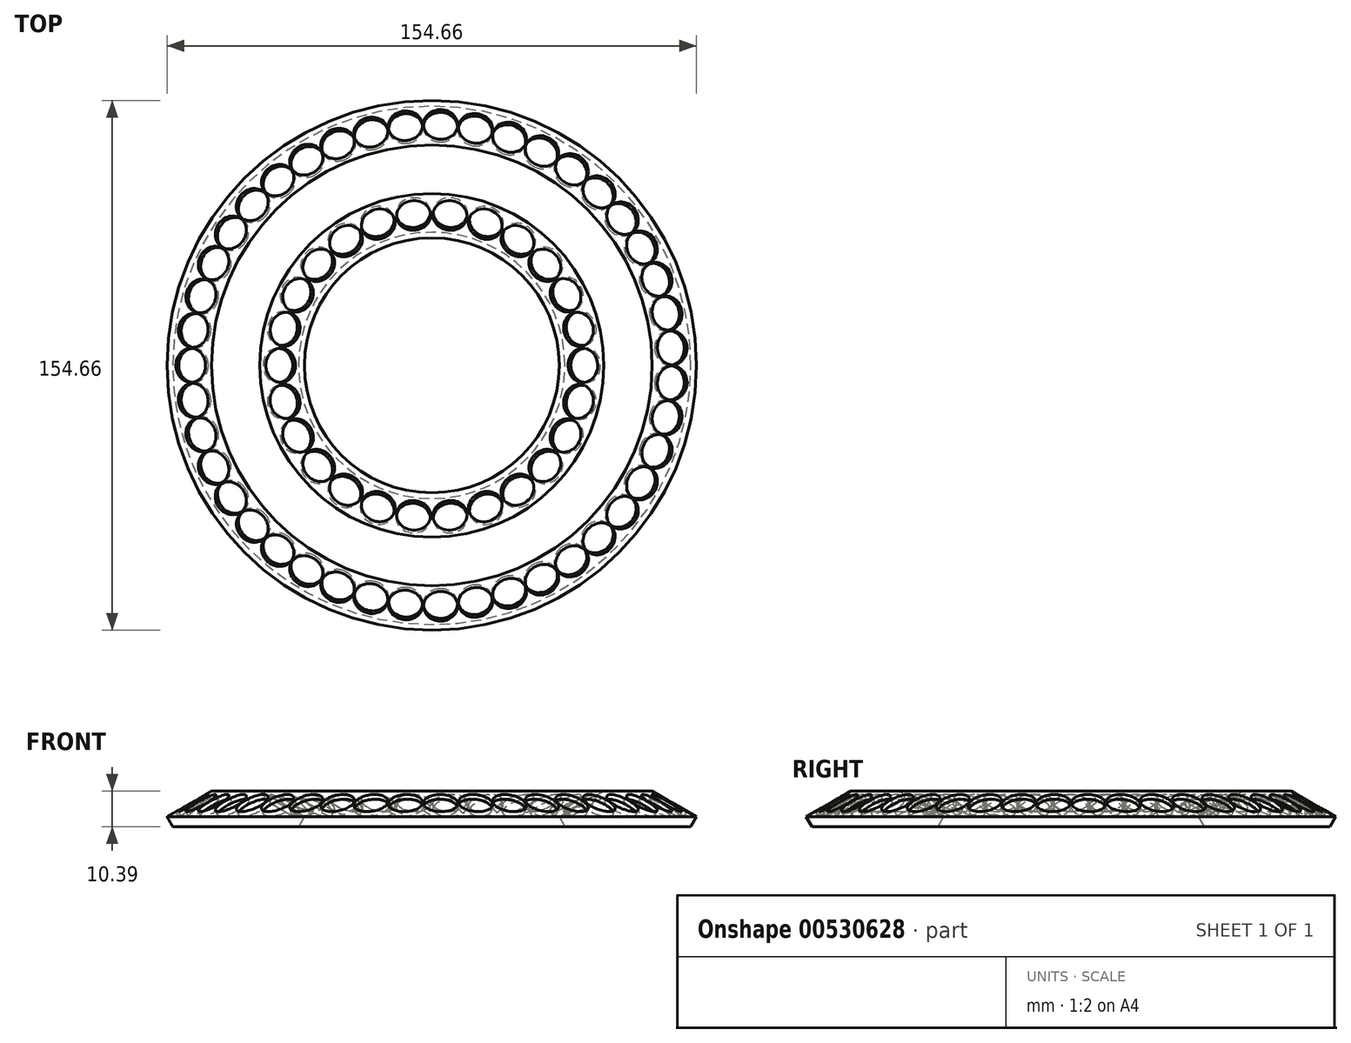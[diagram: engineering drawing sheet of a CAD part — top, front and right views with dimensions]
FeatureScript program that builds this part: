
annotation { "Feature Type Name" : "Feature", "Feature Type Description" : "" }
export const myFeature = defineFeature(function(context is Context, id is Id, definition is map)
    precondition{}
    {
        {
            var Q0;
            Q0=qCreatedBy(makeId("Front.planeOp"),FACE);
            var sketch = newSketch(context, id + "F0", { "sketchPlane" : qUnion([Q0])});
            skLineSegment(sketch, "E0", {"start": v(-82.33, 0) * mm, "end": v(-64.34, 10.39) * mm, "construction": true});
            skLineSegment(sketch, "E1", {"start": v(-64.34, 10.39) * mm, "end": v(-50.2, 10.39) * mm});
            skLineSegment(sketch, "E2", {"start": v(-50.2, 10.39) * mm, "end": v(-32.21, 0) * mm, "construction": true});
            skLineSegment(sketch, "E3", {"start": v(-32.21, 0) * mm, "end": v(-82.33, 0) * mm, "construction": true});
            skLineSegment(sketch, "E4", {"start": v(-48.47, 9.39) * mm, "end": v(-49.27, 8) * mm});
            skLineSegment(sketch, "E5", {"start": v(-49.27, 8) * mm, "end": v(-40.6, 3) * mm});
            skLineSegment(sketch, "E6", {"start": v(-40.6, 3) * mm, "end": v(-39.8, 4.39) * mm});
            skLineSegment(sketch, "E7", {"start": v(-66.07, 9.39) * mm, "end": v(-65.27, 8) * mm});
            skLineSegment(sketch, "E8", {"start": v(-65.27, 8) * mm, "end": v(-73.93, 3) * mm});
            skLineSegment(sketch, "E9", {"start": v(-73.93, 3) * mm, "end": v(-74.73, 4.39) * mm});
            skLineSegment(sketch, "E10", {"start": v(-37.21, 2.89) * mm, "end": v(-38.88, 0) * mm});
            skLineSegment(sketch, "E11", {"start": v(-37.21, 2.89) * mm, "end": v(-50.2, 10.39) * mm});
            skLineSegment(sketch, "E12", {"start": v(-77.33, 2.89) * mm, "end": v(-75.66, 0) * mm});
            skLineSegment(sketch, "E13", {"start": v(-77.33, 2.89) * mm, "end": v(-64.34, 10.39) * mm});
            skLineSegment(sketch, "E14", {"start": v(-57.27, 10.39) * mm, "end": v(-57.27, 7.89) * mm});
            skLineSegment(sketch, "E15", {"start": v(-57.27, 7.89) * mm, "end": v(-56.07, 7.89) * mm});
            skLineSegment(sketch, "E16", {"start": v(-56.07, 7.89) * mm, "end": v(-56.07, 10.39) * mm});
            skLineSegment(sketch, "E17", {"start": v(-69.6, 5.5) * mm, "end": v(-70.4, 6.89) * mm});
            skLineSegment(sketch, "E18", {"start": v(-44.94, 5.5) * mm, "end": v(-44.14, 6.89) * mm});
            skLineSegment(sketch, "E19", {"start": v(-75.66, 0) * mm, "end": v(-38.88, 0) * mm});
            skPoint(sketch, "E20", {"position": v(-70, 6.2) * mm});
            skPoint(sketch, "E21", {"position": v(-44.54, 6.2) * mm});
            skLineSegment(sketch, "E22", {"start": v(0, 0) * mm, "end": v(0, 19.86) * mm, "construction": true});
            skLineSegment(sketch, "E23", {"start": v(-48.47, 9.39) * mm, "end": v(-46.18, 13.36) * mm});
            skLineSegment(sketch, "E24", {"start": v(-46.18, 13.36) * mm, "end": v(-37.52, 8.36) * mm});
            skLineSegment(sketch, "E25", {"start": v(-37.52, 8.36) * mm, "end": v(-39.8, 4.39) * mm});
            skLineSegment(sketch, "E26", {"start": v(-44.14, 6.89) * mm, "end": v(-41.85, 10.86) * mm});
            skSolve(sketch);
        }
        {
            var Q0;
            {var subQ0=sQuery(id+"F0.wireOp",EDGE,"E7");Q0=makeQuery(id+"F0.imprint","IMPRINT",FACE,{"disambiguationData":[TD([[makeQuery(id+"F0.imprint","IMPRINT",EDGE,{"derivedFrom":subQ0}),-1.0]])]});}
            var Q1;
            {var subQ11=sQuery(id+"F0.wireOp",EDGE,"E4");Q1=makeQuery(id+"F0.imprint","IMPRINT",FACE,{"disambiguationData":[TD([[makeQuery(id+"F0.imprint","IMPRINT",EDGE,{"derivedFrom":subQ11}),-1.0]])]});}
            var Q2;
            {var subQ0=sQuery(id+"F0.wireOp",EDGE,"E4");Q2=makeQuery(id+"F0.imprint","IMPRINT",FACE,{"disambiguationData":[TD([[makeQuery(id+"F0.imprint","IMPRINT",EDGE,{"derivedFrom":subQ0}),1.0]])]});}
            var Q3;
            {var subQ0=sQuery(id+"F0.wireOp",EDGE,"E14");Q3=makeQuery(id+"F0.imprint","IMPRINT",FACE,{"disambiguationData":[TD([[makeQuery(id+"F0.imprint","IMPRINT",EDGE,{"derivedFrom":subQ0}),1.0]])]});}
            var Q4;
            {var subQ0=sQuery(id+"F0.wireOp",EDGE,"E9");Q4=makeQuery(id+"F0.imprint","IMPRINT",FACE,{"disambiguationData":[TD([[makeQuery(id+"F0.imprint","IMPRINT",EDGE,{"derivedFrom":subQ0}),-1.0]])]});}
            var Q5;
            {var subQ0=sQuery(id+"F0.wireOp",EDGE,"E6");Q5=makeQuery(id+"F0.imprint","IMPRINT",FACE,{"disambiguationData":[TD([[makeQuery(id+"F0.imprint","IMPRINT",EDGE,{"derivedFrom":subQ0}),1.0]])]});}
            var Q6;
            Q6=sQuery(id+"F0.wireOp",EDGE,"E22");
            revolve(context, id + "F1", {"entities" : qUnion([Q0, Q1, Q2, Q3, Q4, Q5]), "axis" : qUnion([Q6]), "revolveType" : RevolveType.FULL});
        }
        {
            var Q0;
            {var subQ0=sQuery(id+"F0.wireOp",EDGE,"E9");Q0=makeQuery(id+"F0.imprint","IMPRINT",FACE,{"disambiguationData":[TD([[makeQuery(id+"F0.imprint","IMPRINT",EDGE,{"derivedFrom":subQ0}),-1.0]])]});}
            var Q1;
            Q1=sQuery(id+"F0.wireOp",EDGE,"E17");
            revolve(context, id + "F2", {"entities" : qUnion([Q0]), "axis" : qUnion([Q1]), "revolveType" : RevolveType.FULL, "oppositeDirection" : true});
        }
        {
            var Q0;
            {var subQ0=sQuery(id+"F0.wireOp",EDGE,"E6");Q0=makeQuery(id+"F0.imprint","IMPRINT",FACE,{"disambiguationData":[TD([[makeQuery(id+"F0.imprint","IMPRINT",EDGE,{"derivedFrom":subQ0}),1.0]])]});}
            var Q1;
            {var subQ0=sQuery(id+"F0.wireOp",EDGE,"E25");Q1=makeQuery(id+"F0.imprint","IMPRINT",FACE,{"disambiguationData":[TD([[makeQuery(id+"F0.imprint","IMPRINT",EDGE,{"derivedFrom":subQ0}),-1.0]])]});}
            var Q2;
            Q2=sQuery(id+"F0.wireOp",EDGE,"E18");
            revolve(context, id + "F3", {"entities" : qUnion([Q0, Q1]), "axis" : qUnion([Q2]), "revolveType" : RevolveType.FULL, "oppositeDirection" : true});
        }
        {
            var Q0;
            Q0=makeQuery(id+"F2.opRevolve","SWEPT_BODY",BODY,{"disambiguationData":[OSD([sQuery(id+"F0.wireOp",EDGE,"E8"),sQuery(id+"F0.wireOp",EDGE,"E9"),sQuery(id+"F0.wireOp",EDGE,"E13"),sQuery(id+"F0.wireOp",EDGE,"E17")])]});
            var Q1;
            Q1=sQuery(id+"F0.wireOp",EDGE,"E22");
            circularPattern(context, id + "F4", {"operationType" : NewBodyOperationType.REMOVE, "entities" : qUnion([Q0]), "axis" : qUnion([Q1]), "angle" : 360 * degree, "instanceCount" : 43, "equalSpace" : true});
        }
        {
            var Q0;
            Q0=makeQuery(id+"F3.opRevolve","SWEPT_BODY",BODY,{"disambiguationData":[OSD([sQuery(id+"F0.wireOp",EDGE,"E5"),sQuery(id+"F0.wireOp",EDGE,"E6"),sQuery(id+"F0.wireOp",EDGE,"E18"),sQuery(id+"F0.wireOp",EDGE,"E24"),sQuery(id+"F0.wireOp",EDGE,"E25"),sQuery(id+"F0.wireOp",EDGE,"E26")])]});
            var Q1;
            Q1=sQuery(id+"F0.wireOp",EDGE,"E22");
            circularPattern(context, id + "F5", {"operationType" : NewBodyOperationType.REMOVE, "entities" : qUnion([Q0]), "axis" : qUnion([Q1]), "angle" : 360 * degree, "instanceCount" : 26, "equalSpace" : true});
        }
    });
